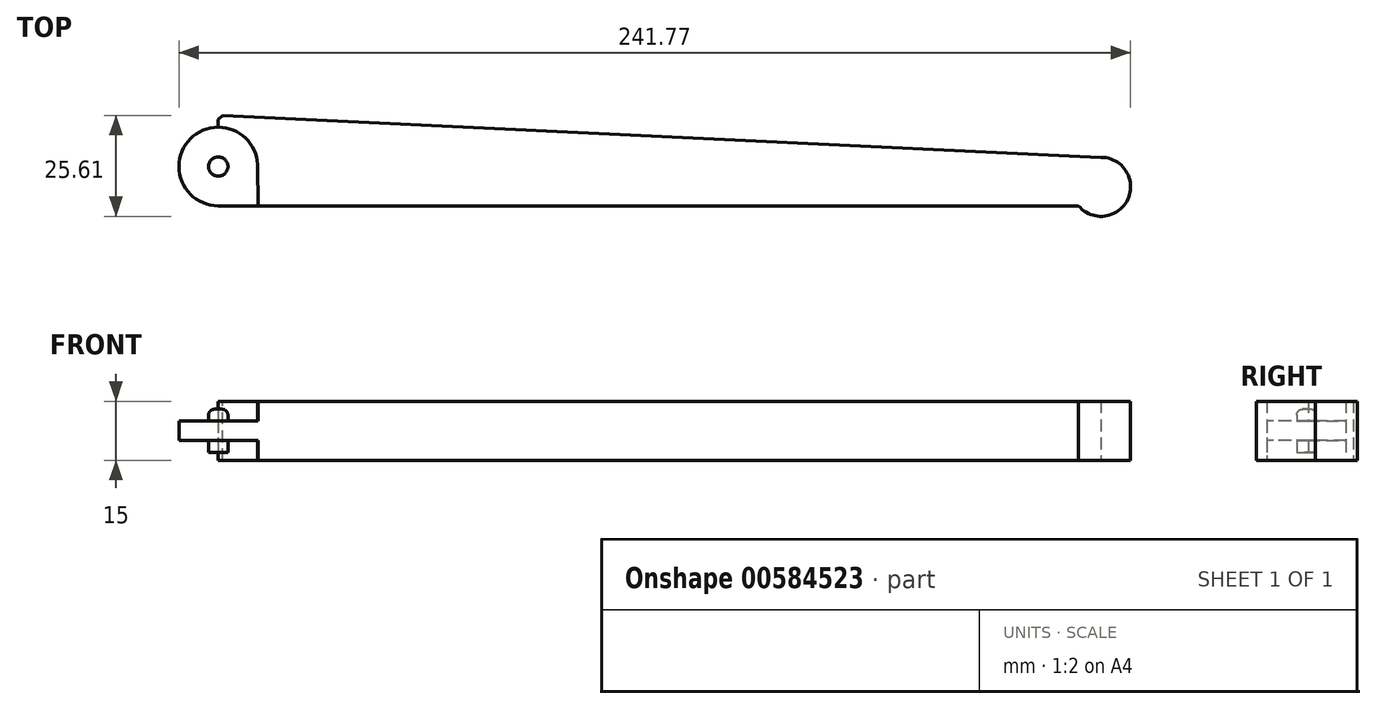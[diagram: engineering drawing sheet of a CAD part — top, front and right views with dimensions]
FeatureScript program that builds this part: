
annotation { "Feature Type Name" : "Feature", "Feature Type Description" : "" }
export const myFeature = defineFeature(function(context is Context, id is Id, definition is map)
    precondition{}
    {
        {
            var Q0;
            Q0=qCreatedBy(makeId("Top.planeOp"),FACE);
            var sketch = newSketch(context, id + "F0", { "sketchPlane" : qUnion([Q0])});
            skPoint(sketch, "E0.middle", {"position": v(0, 0) * mm});
            skLineSegment(sketch, "E1", {"start": v(-112.45, 0) * mm, "end": v(106.1, 0) * mm});
            skArc(sketch, "E2", {"start": v(106.1, 0) * mm, "mid": v(118.62, 1.68) * mm, "end": v(111.82, 12.34) * mm});
            skArc(sketch, "E3", {"start": v(-112.45, 20) * mm, "mid": v(-122.45, 10) * mm, "end": v(-112.45, 0) * mm});
            skPoint(sketch, "E4.orphan", {"position": v(117.55, 0) * mm});
            skLineSegment(sketch, "E5", {"start": v(-112.45, 20) * mm, "end": v(-112.45, 23) * mm});
            skLineSegment(sketch, "E6", {"start": v(-112.45, 23) * mm, "end": v(111.82, 12.34) * mm});
            skSolve(sketch);
        }
        {
            var Q0;
            Q0 = qSketchRegion(id + "F0", true);
            extrude(context, id + "F1", {"entities" : qUnion([Q0]), "depth" : 15 * mm, "offsetDistance" : 25 * mm});
        }
        {
            var Q0;
            Q0=qCreatedBy(makeId("Top.planeOp"),FACE);
            var sketch = newSketch(context, id + "F2", { "sketchPlane" : qUnion([Q0])});
            skPoint(sketch, "E7.0", {"position": v(-112.45, 10) * mm});
            skArc(sketch, "E8", {"start": v(-102.46, 10.48) * mm, "mid": v(-119.69, 16.9) * mm, "end": v(-112.45, 0) * mm});
            skCircle(sketch, "E9", {"center": v(-112.45, 10) * mm, "radius": 2.45 * mm});
            skLineSegment(sketch, "E10", {"start": v(-102.46, 10.48) * mm, "end": v(-102.28, 0) * mm});
            skLineSegment(sketch, "E11", {"start": v(-102.28, 0) * mm, "end": v(-112.45, 0) * mm});
            skSolve(sketch);
        }
        {
            var Q0;
            Q0 = qSketchRegion(id + "F2", true);
            extrude(context, id + "F3", {"entities" : qUnion([Q0]), "operationType" : NewBodyOperationType.REMOVE, "depth" : 5 * mm, "offsetDistance" : 25 * mm});
        }
        {
            var Q0;
            Q0 = qSketchRegion(id + "F2", true);
            extrude(context, id + "F4", {"entities" : qUnion([Q0]), "operationType" : NewBodyOperationType.REMOVE, "endBound" : BoundingType.UP_TO_NEXT, "depth" : 10 * mm, "hasOffset" : true, "offsetDistance" : 10 * mm, "offsetOppositeDirection" : true, "hasSecondDirection" : true, "secondDirectionOppositeDirection" : false, "secondDirectionDepth" : 10 * mm});
        }
        {
            var Q0;
            Q0=makeQuery(id+"F4.boolean.opBoolean","SPLIT",FACE,{"disambiguationData":[TD([makeQuery(id+"F4.opExtrude","SWEPT_FACE",FACE,{"disambiguationData":[OSD([sQuery(id+"F2.wireOp",EDGE,"E9")])]})])],"derivedFrom":makeQuery(id+"F1.opExtrude","CAP_FACE",FACE,{"disambiguationData":[OSD([sQuery(id+"F0.wireOp",EDGE,"E1"),sQuery(id+"F0.wireOp",EDGE,"E2"),sQuery(id+"F0.wireOp",EDGE,"E3"),sQuery(id+"F0.wireOp",EDGE,"ICITt8e3-zTpg-WYht-18EF-VDJriyI8qyvp"),sQuery(id+"F0.wireOp",EDGE,"QLlQdMzX-Z1Ki-qbhD-PUhB-xGOlY88uPTue")])],"isStart":false})});
            extrude(context, id + "F5", {"entities" : qUnion([Q0]), "operationType" : NewBodyOperationType.REMOVE, "oppositeDirection" : true, "depth" : 2 * mm, "offsetDistance" : 25 * mm});
        }
        {
            var Q0;
            Q0=makeQuery(id+"F3.boolean.opBoolean","SPLIT",FACE,{"disambiguationData":[TD([makeQuery(id+"F3.opExtrude","SWEPT_FACE",FACE,{"disambiguationData":[OSD([sQuery(id+"F2.wireOp",EDGE,"E9")])]})])],"derivedFrom":makeQuery(id+"F1.opExtrude","CAP_FACE",FACE,{"disambiguationData":[OSD([sQuery(id+"F0.wireOp",EDGE,"E1"),sQuery(id+"F0.wireOp",EDGE,"E2"),sQuery(id+"F0.wireOp",EDGE,"E3"),sQuery(id+"F0.wireOp",EDGE,"ICITt8e3-zTpg-WYht-18EF-VDJriyI8qyvp"),sQuery(id+"F0.wireOp",EDGE,"QLlQdMzX-Z1Ki-qbhD-PUhB-xGOlY88uPTue")])],"isStart":true})});
            extrude(context, id + "F6", {"entities" : qUnion([Q0]), "operationType" : NewBodyOperationType.REMOVE, "oppositeDirection" : true, "depth" : 2 * mm, "offsetDistance" : 25 * mm});
        }
        {
            var Q0;
            Q0=makeQuery(id+"F5.boolean.opBoolean","COPY",FACE,{"derivedFrom":makeQuery(id+"F5.opExtrude","CAP_FACE",FACE,{"disambiguationData":[OSD([sQuery(id+"F0.wireOp",EDGE,"E1"),sQuery(id+"F0.wireOp",EDGE,"E2"),sQuery(id+"F0.wireOp",EDGE,"E3"),sQuery(id+"F0.wireOp",EDGE,"ICITt8e3-zTpg-WYht-18EF-VDJriyI8qyvp"),sQuery(id+"F0.wireOp",EDGE,"QLlQdMzX-Z1Ki-qbhD-PUhB-xGOlY88uPTue")])],"isStart":false})});
            var Q1;
            Q1=makeQuery(id+"F6.boolean.opBoolean","COPY",EDGE,{"derivedFrom":makeQuery(id+"F6.opExtrude","CAP_EDGE",EDGE,{"disambiguationData":[OSD([sQuery(id+"F2.wireOp",EDGE,"E9")])],"isStart":false})});
            fillet(context, id + "F7", {"entities" : qUnion([Q0, Q1]), "radius" : 1.5 * mm, "tangentPropagation" : true, "allowEdgeOverflow" : false});
        }
        {
            var Q0;
            Q0=makeQuery(id+"F1.opExtrude","SWEPT_EDGE",EDGE,{"disambiguationData":[OSD([sQuery(id+"F0.wireOp",EDGE,"E5"),sQuery(id+"F0.wireOp",EDGE,"E6")])]});
            chamfer(context, id + "F8", {"entities" : qUnion([Q0]), "width" : 1 * mm, "tangentPropagation" : true});
        }
    });
